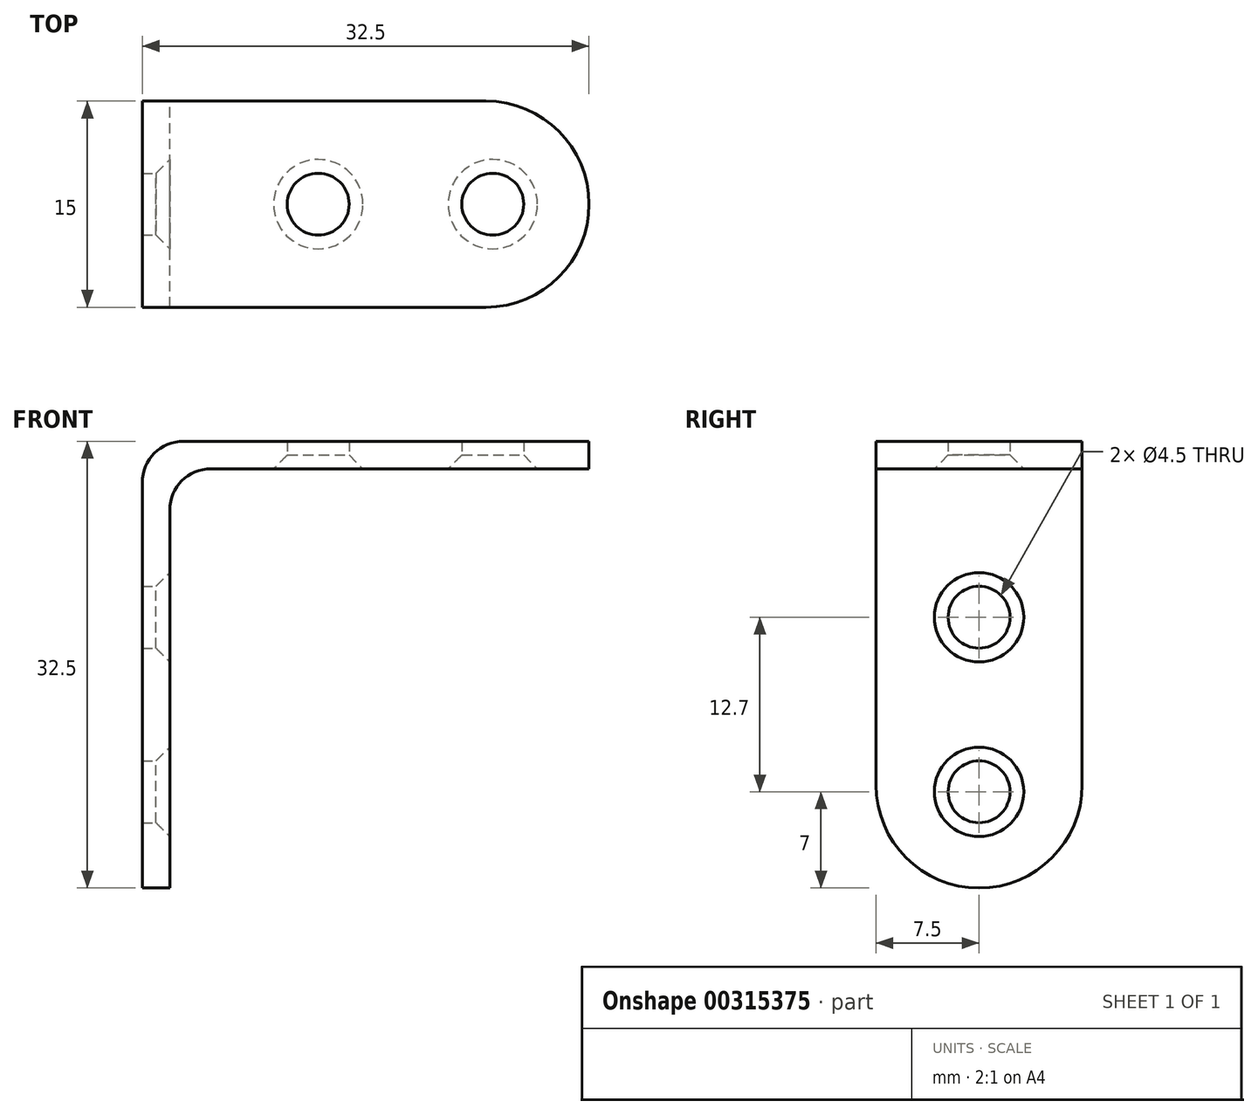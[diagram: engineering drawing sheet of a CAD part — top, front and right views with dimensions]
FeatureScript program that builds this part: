
annotation { "Feature Type Name" : "Feature", "Feature Type Description" : "" }
export const myFeature = defineFeature(function(context is Context, id is Id, definition is map)
    precondition{}
    {
        {
            var Q0;
            Q0=qCreatedBy(makeId("Front.planeOp"),FACE);
            var sketch = newSketch(context, id + "F0", { "sketchPlane" : qUnion([Q0])});
            skLineSegment(sketch, "E0", {"start": v(0, -32.5) * mm, "end": v(0, 0) * mm});
            skLineSegment(sketch, "E1", {"start": v(0, 0) * mm, "end": v(32.5, 0) * mm});
            skLineSegment(sketch, "E2", {"start": v(32.5, 0) * mm, "end": v(32.5, -2) * mm});
            skLineSegment(sketch, "E3", {"start": v(32.5, -2) * mm, "end": v(2, -2) * mm});
            skLineSegment(sketch, "E4", {"start": v(2, -2) * mm, "end": v(2, -32.5) * mm});
            skLineSegment(sketch, "E5", {"start": v(2, -32.5) * mm, "end": v(0, -32.5) * mm});
            skSolve(sketch);
        }
        {
            var Q0;
            Q0 = qSketchRegion(id + "F0", true);
            extrude(context, id + "F1", {"entities" : qUnion([Q0]), "endBound" : BoundingType.SYMMETRIC, "depth" : 15 * mm});
        }
        {
            var Q0;
            Q0=makeQuery(id+"F1.opExtrude","CAP_EDGE",EDGE,{"disambiguationData":[OSD([sQuery(id+"F0.wireOp",EDGE,"E2")])],"isStart":false});
            var Q1;
            Q1=makeQuery(id+"F1.opExtrude","CAP_EDGE",EDGE,{"disambiguationData":[OSD([sQuery(id+"F0.wireOp",EDGE,"E2")])],"isStart":true});
            var Q2;
            Q2=makeQuery(id+"F1.opExtrude","CAP_EDGE",EDGE,{"disambiguationData":[OSD([sQuery(id+"F0.wireOp",EDGE,"E5")])],"isStart":false});
            var Q3;
            Q3=makeQuery(id+"F1.opExtrude","CAP_EDGE",EDGE,{"disambiguationData":[OSD([sQuery(id+"F0.wireOp",EDGE,"E5")])],"isStart":true});
            fillet(context, id + "F2", {"entities" : qUnion([Q0, Q1, Q2, Q3]), "radius" : 7.5 * mm, "tangentPropagation" : true, "allowEdgeOverflow" : false});
        }
        {
            var Q0;
            Q0=makeQuery(id+"F1.opExtrude","SWEPT_EDGE",EDGE,{"disambiguationData":[OSD([sQuery(id+"F0.wireOp",EDGE,"E3"),sQuery(id+"F0.wireOp",EDGE,"E4")])]});
            var Q1;
            Q1=makeQuery(id+"F1.opExtrude","SWEPT_EDGE",EDGE,{"disambiguationData":[OSD([sQuery(id+"F0.wireOp",EDGE,"E0"),sQuery(id+"F0.wireOp",EDGE,"E1")])]});
            fillet(context, id + "F3", {"entities" : qUnion([Q0, Q1]), "radius" : 3 * mm, "tangentPropagation" : true, "allowEdgeOverflow" : false});
        }
        {
            var Q0;
            Q0=makeQuery(id+"F1.opExtrude","SWEPT_FACE",FACE,{"disambiguationData":[OSD([sQuery(id+"F0.wireOp",EDGE,"E3")])]});
            var sketch = newSketch(context, id + "F4", { "sketchPlane" : qUnion([Q0])});
            skPoint(sketch, "E6", {"position": v(25.5, 0) * mm});
            skPoint(sketch, "E7", {"position": v(12.8, 0) * mm});
            skSolve(sketch);
        }
        {
            var Q0;
            Q0=makeQuery(id+"F1.opExtrude","SWEPT_FACE",FACE,{"disambiguationData":[OSD([sQuery(id+"F0.wireOp",EDGE,"E4")])]});
            var sketch = newSketch(context, id + "F5", { "sketchPlane" : qUnion([Q0])});
            skPoint(sketch, "E8", {"position": v(0, -25.5) * mm});
            skPoint(sketch, "E9", {"position": v(0, -12.8) * mm});
            skSolve(sketch);
        }
        {
            var Q0;
            Q0=sQuery(id+"F4.wireOp",VERTEX,"E7");
            var Q1;
            Q1=sQuery(id+"F4.wireOp",VERTEX,"E6");
            var Q2;
            Q2=sQuery(id+"F5.wireOp",VERTEX,"E8");
            var Q3;
            Q3=sQuery(id+"F5.wireOp",VERTEX,"E9");
            var Q4;
            Q4=makeQuery(id+"F1.opExtrude","SWEPT_BODY",BODY,{"disambiguationData":[OSD([sQuery(id+"F0.wireOp",EDGE,"E0"),sQuery(id+"F0.wireOp",EDGE,"E1"),sQuery(id+"F0.wireOp",EDGE,"E2"),sQuery(id+"F0.wireOp",EDGE,"E3"),sQuery(id+"F0.wireOp",EDGE,"E4"),sQuery(id+"F0.wireOp",EDGE,"E5")])]});
            hole(context, id + "F6", {"style" : HoleStyle.C_SINK, "endStyle" : HoleEndStyle.THROUGH, "holeDiameter" : 4.5 * mm, "cSinkDiameter" : 6.5 * mm, "cSinkAngle" : 90 * degree, "tappedDepth" : 4.2 * mm, "tapClearance" : 3, "locations" : qUnion([Q0, Q1, Q2, Q3]), "scope" : qUnion([Q4])});
        }
    });
